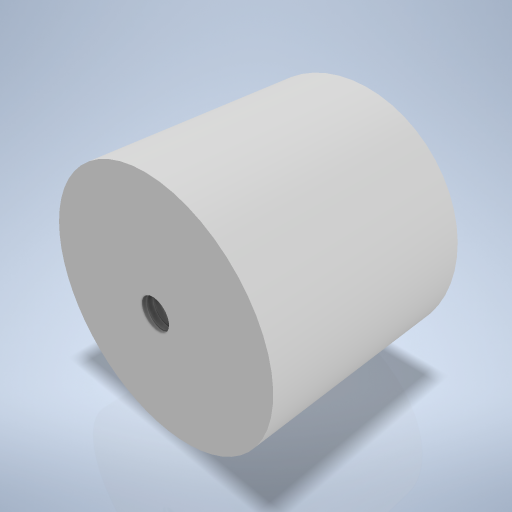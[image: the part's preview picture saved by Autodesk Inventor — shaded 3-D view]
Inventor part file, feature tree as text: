
AUTODESK INVENTOR PART (.ipt)
format: ipt  version: 2024.2 (Build 282272000, 272)  size: 221,696 bytes
history: native  units: mm
features: sketch x3, extrude x2, hole x1
ambient origin geometry x8: Origin, YZ Plane, XZ Plane, XY Plane, X Axis, Y Axis, Z Axis, Center Point
bodies: Volumenkörper1 (feature_tree)
feature tree (6):
  extrude  "Extrusion1"  Depth=16.5mm TaperAngle=0.0deg
  extrude  "Extrusion2"  Depth=15.0mm TaperAngle=0.0deg
  hole  "Bohrung1"  [1 undecoded]
  sketch  "Skizze1"  dims[d0=19.0mm d1=16.5mm d2=0.0mm]
  sketch  "Skizze2"  dims[d3=16.0mm d4=15.0mm d5=0.0mm]
  sketch  "Skizze3"  dims[d6=2.459mm d7=1.5mm d8=4.0mm d9=2.0mm d10=90.0deg d11=1.5mm d12=0.0mm]
note: 1 required parameter value undecoded (feature->parameter linkage not recoverable at this tier; creation-order binding heuristic only, values carry confidence <= 0.55)
